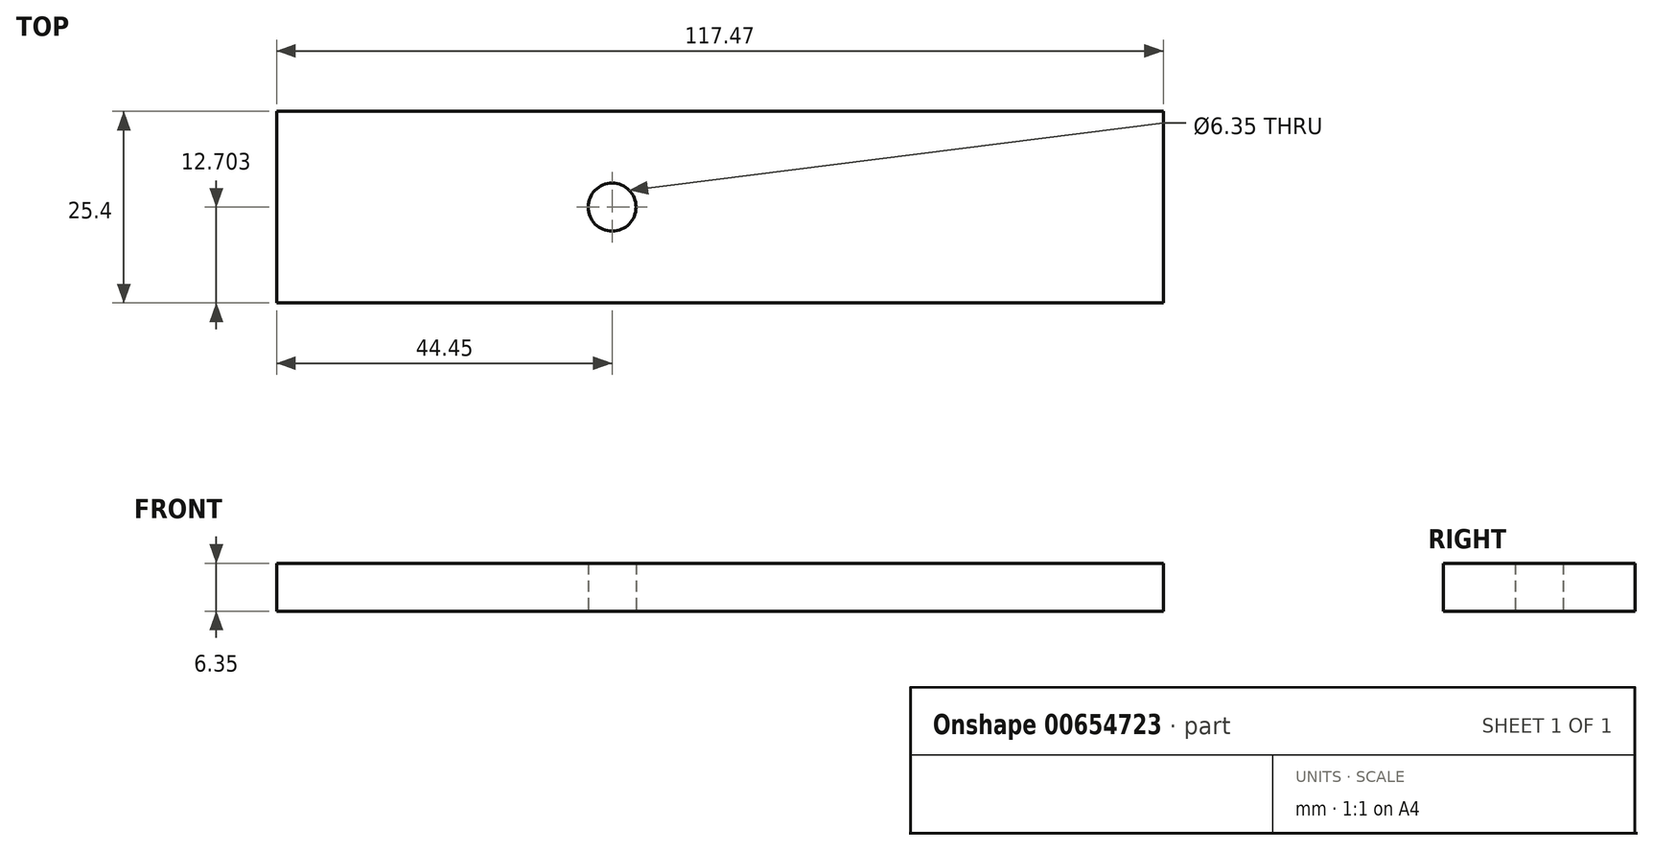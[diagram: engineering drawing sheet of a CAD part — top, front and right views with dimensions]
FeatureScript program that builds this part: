
annotation { "Feature Type Name" : "Feature", "Feature Type Description" : "" }
export const myFeature = defineFeature(function(context is Context, id is Id, definition is map)
    precondition{}
    {
        {
            var Q0;
            Q0=qCreatedBy(makeId("Top.planeOp"),FACE);
            var sketch = newSketch(context, id + "F0", { "sketchPlane" : qUnion([Q0])});
            skLineSegment(sketch, "E0.bottom", {"start": v(-26.38, -2.57) * mm, "end": v(91.1, -2.57) * mm});
            skLineSegment(sketch, "E0.top", {"start": v(-26.38, 22.83) * mm, "end": v(91.1, 22.83) * mm});
            skLineSegment(sketch, "E0.left", {"start": v(-26.38, -2.57) * mm, "end": v(-26.38, 22.83) * mm});
            skLineSegment(sketch, "E0.right", {"start": v(91.1, -2.57) * mm, "end": v(91.1, 22.83) * mm});
            skCircle(sketch, "E1", {"center": v(18.07, 10.13) * mm, "radius": 3.18 * mm});
            skSolve(sketch);
        }
        {
            var Q0;
            Q0 = qSketchRegion(id + "F0", true);
            extrude(context, id + "F1", {"entities" : qUnion([Q0]), "depth" : 6.35 * mm, "offsetDistance" : 25.4 * mm});
        }
    });
